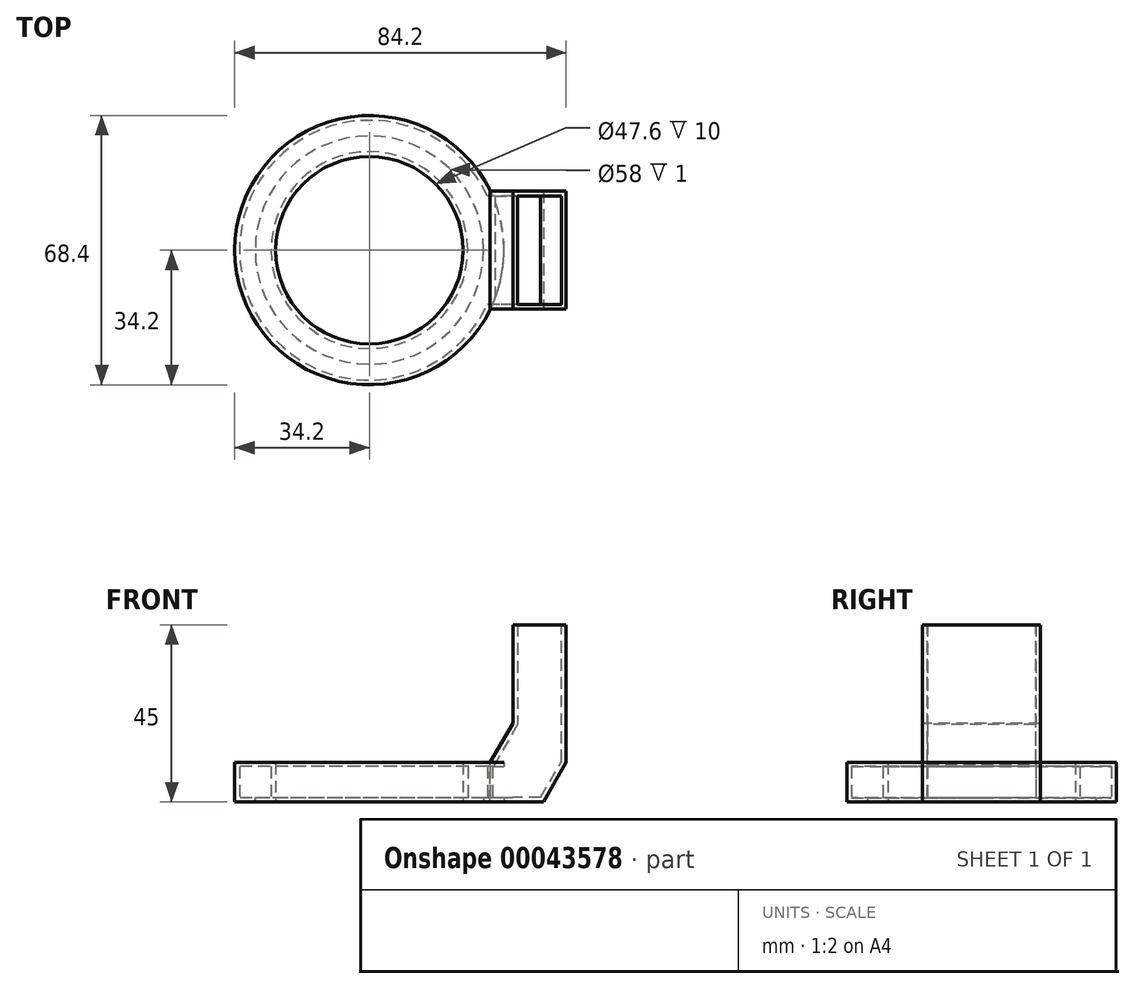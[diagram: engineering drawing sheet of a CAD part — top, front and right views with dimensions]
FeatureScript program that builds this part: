
annotation { "Feature Type Name" : "Feature", "Feature Type Description" : "" }
export const myFeature = defineFeature(function(context is Context, id is Id, definition is map)
    precondition{}
    {
        {
            var Q0;
            Q0=qCreatedBy(makeId("Top.planeOp"),FACE);
            var sketch = newSketch(context, id + "F0", { "sketchPlane" : qUnion([Q0])});
            skCircle(sketch, "E0", {"center": v(0, 0) * mm, "radius": 25 * mm});
            skCircle(sketch, "E1", {"center": v(0, 0) * mm, "radius": 33 * mm});
            skCircle(sketch, "E2", {"center": v(0, 0) * mm, "radius": 34.2 * mm});
            skCircle(sketch, "E3", {"center": v(0, 0) * mm, "radius": 23.8 * mm});
            skCircle(sketch, "E4", {"center": v(0, 0) * mm, "radius": 29 * mm});
            skSolve(sketch);
        }
        {
            var Q0;
            Q0=makeQuery(id+"F0.imprint","IMPRINT",FACE,{"disambiguationData":[TD([[makeQuery(id+"F0.imprint","IMPRINT",EDGE,{"derivedFrom":sQuery(id+"F0.wireOp",EDGE,"E0")}),-1.0]])]});
            var Q1;
            Q1=makeQuery(id+"F0.imprint","IMPRINT",FACE,{"disambiguationData":[TD([[makeQuery(id+"F0.imprint","IMPRINT",EDGE,{"derivedFrom":sQuery(id+"F0.wireOp",EDGE,"E1")}),1.0]])]});
            extrude(context, id + "F1", {"entities" : qUnion([Q0, Q1]), "depth" : 10 * mm, "hasSecondDirection" : true, "secondDirectionOppositeDirection" : false, "secondDirectionDepth" : 9 * mm});
        }
        {
            var Q0;
            Q0=makeQuery(id+"F0.imprint","IMPRINT",FACE,{"disambiguationData":[TD([[makeQuery(id+"F0.imprint","IMPRINT",EDGE,{"derivedFrom":sQuery(id+"F0.wireOp",EDGE,"E1")}),-1.0]])]});
            var Q1;
            Q1=makeQuery(id+"F0.imprint","IMPRINT",FACE,{"disambiguationData":[TD([[makeQuery(id+"F0.imprint","IMPRINT",EDGE,{"derivedFrom":sQuery(id+"F0.wireOp",EDGE,"E0")}),1.0]])]});
            extrude(context, id + "F2", {"entities" : qUnion([Q0, Q1]), "operationType" : NewBodyOperationType.ADD, "depth" : 10 * mm});
        }
        {
            var Q0;
            Q0=makeQuery(id+"F0.imprint","IMPRINT",FACE,{"disambiguationData":[TD([[makeQuery(id+"F0.imprint","IMPRINT",EDGE,{"derivedFrom":sQuery(id+"F0.wireOp",EDGE,"E1")}),1.0]])]});
            extrude(context, id + "F3", {"entities" : qUnion([Q0]), "operationType" : NewBodyOperationType.ADD, "depth" : 1 * mm});
        }
        {
            var Q0;
            Q0=qCreatedBy(makeId("Right.planeOp"),FACE);
            var sketch = newSketch(context, id + "F4", { "sketchPlane" : qUnion([Q0])});
            skLineSegment(sketch, "E5.bottom", {"start": v(-15, 0) * mm, "end": v(15, 0) * mm});
            skLineSegment(sketch, "E5.top", {"start": v(-15, 20) * mm, "end": v(15, 20) * mm});
            skLineSegment(sketch, "E5.left", {"start": v(-15, 0) * mm, "end": v(-15, 20) * mm});
            skLineSegment(sketch, "E5.right", {"start": v(15, 0) * mm, "end": v(15, 20) * mm});
            skSolve(sketch);
        }
        {
            var Q0;
            Q0=makeQuery(id+"F4.imprint","IMPRINT",FACE,{"disambiguationData":[TD([[makeQuery(id+"F4.imprint","IMPRINT",EDGE,{"derivedFrom":sQuery(id+"F4.wireOp",EDGE,"E5.bottom")}),1.0]])]});
            extrude(context, id + "F5", {"entities" : qUnion([Q0]), "depth" : 50 * mm, "hasSecondDirection" : true, "secondDirectionOppositeDirection" : false, "secondDirectionDepth" : 30.7 * mm});
        }
        {
            var Q0;
            Q0=makeQuery(id+"F5.opExtrude","CAP_EDGE",EDGE,{"disambiguationData":[OSD([sQuery(id+"F4.wireOp",EDGE,"E5.top")])],"isStart":true});
            var Q1;
            Q1=makeQuery(id+"F5.opExtrude","CAP_EDGE",EDGE,{"disambiguationData":[OSD([sQuery(id+"F4.wireOp",EDGE,"E5.bottom")])],"isStart":false});
            chamfer(context, id + "F6", {"entities" : qUnion([Q0, Q1]), "chamferType" : ChamferType.OFFSET_ANGLE, "width" : 10 * mm, "oppositeDirection" : false, "angle" : 30 * degree, "tangentPropagation" : true});
        }
        {
            var Q0;
            Q0=makeQuery(id+"F5.opExtrude","SWEPT_FACE",FACE,{"disambiguationData":[OSD([sQuery(id+"F4.wireOp",EDGE,"E5.top")])]});
            var sketch = newSketch(context, id + "F7", { "sketchPlane" : qUnion([Q0])});
            skLineSegment(sketch, "E6.bottom", {"start": v(36.47, 15) * mm, "end": v(50, 15) * mm});
            skLineSegment(sketch, "E6.top", {"start": v(36.47, -15) * mm, "end": v(50, -15) * mm});
            skLineSegment(sketch, "E6.left", {"start": v(36.47, 15) * mm, "end": v(36.47, -15) * mm});
            skLineSegment(sketch, "E6.right", {"start": v(50, 15) * mm, "end": v(50, -15) * mm});
            skSolve(sketch);
        }
        {
            var Q0;
            Q0 = qSketchRegion(id + "F7", true);
            var Q1;
            Q1=makeQuery(id+"F7.imprint","IMPRINT",FACE,{"disambiguationData":[TD([[makeQuery(id+"F7.imprint","IMPRINT",EDGE,{"derivedFrom":sQuery(id+"F7.wireOp",EDGE,"E6.bottom")}),1.0]])]});
            extrude(context, id + "F8", {"entities" : qUnion([Q0, Q1]), "operationType" : NewBodyOperationType.ADD, "depth" : 25 * mm});
        }
        {
            var Q0;
            Q0=makeQuery(id+"F5.opExtrude","SWEPT_FACE",FACE,{"disambiguationData":[OSD([sQuery(id+"F4.wireOp",EDGE,"E5.top")])]});
            var Q1;
            Q1=makeQuery(id+"F8.opExtrude","CAP_FACE",FACE,{"disambiguationData":[OSD([sQuery(id+"F7.wireOp",EDGE,"E6.bottom"),sQuery(id+"F7.wireOp",EDGE,"E6.top"),sQuery(id+"F7.wireOp",EDGE,"E6.left"),sQuery(id+"F7.wireOp",EDGE,"E6.right")])],"isStart":false});
            var Q2;
            Q2=makeQuery(id+"F5.opExtrude","SWEPT_BODY",BODY,{"disambiguationData":[OSD([sQuery(id+"F4.wireOp",EDGE,"E5.bottom"),sQuery(id+"F4.wireOp",EDGE,"E5.top"),sQuery(id+"F4.wireOp",EDGE,"E5.left"),sQuery(id+"F4.wireOp",EDGE,"E5.right")])]});
            shell(context, id + "F9", {"entities" : qUnion([Q0, Q1]), "parts" : qUnion([Q2]), "thickness" : 1.2 * mm});
        }
        {
            var Q0;
            Q0=qCreatedBy(makeId("Right.planeOp"),FACE);
            var sketch = newSketch(context, id + "F10", { "sketchPlane" : qUnion([Q0])});
            skLineSegment(sketch, "E7.bottom", {"start": v(-13.8, 0) * mm, "end": v(0, 0) * mm});
            skLineSegment(sketch, "E7.top", {"start": v(-13.8, 9) * mm, "end": v(13.8, 9) * mm});
            skLineSegment(sketch, "E7.left", {"start": v(-13.8, 0) * mm, "end": v(-13.8, 9) * mm});
            skLineSegment(sketch, "E7.right", {"start": v(13.8, 0) * mm, "end": v(13.8, 9) * mm});
            skLineSegment(sketch, "E8", {"start": v(0, 0) * mm, "end": v(13.8, 0) * mm});
            skLineSegment(sketch, "E9", {"start": v(-13.8, 1) * mm, "end": v(13.8, 1) * mm});
            skSolve(sketch);
        }
        {
            var Q0;
            {var subQ2=sQuery(id+"F10.wireOp",EDGE,"E7.top");Q0=makeQuery(id+"F10.imprint","IMPRINT",FACE,{"disambiguationData":[TD([[makeQuery(id+"F10.imprint","IMPRINT",EDGE,{"derivedFrom":subQ2}),-1.0]])]});}
            extrude(context, id + "F11", {"entities" : qUnion([Q0]), "operationType" : NewBodyOperationType.REMOVE, "depth" : 36.4 * mm, "hasSecondDirection" : true, "secondDirectionOppositeDirection" : false, "secondDirectionDepth" : 27.83 * mm});
        }
    });
